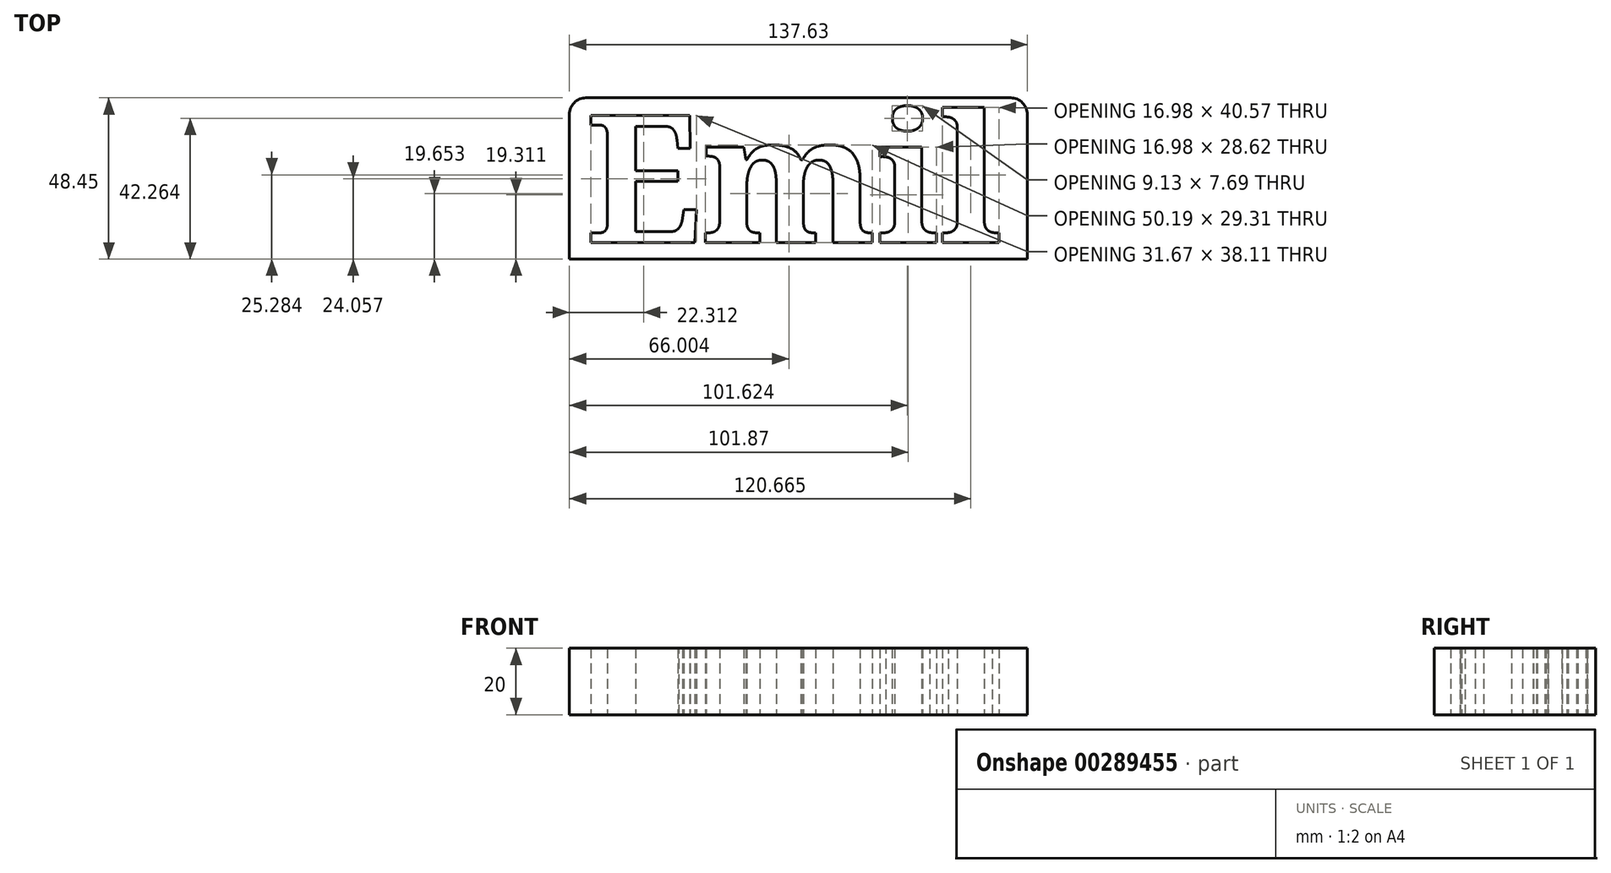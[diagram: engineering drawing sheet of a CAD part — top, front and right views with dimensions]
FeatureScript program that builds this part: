
annotation { "Feature Type Name" : "Feature", "Feature Type Description" : "" }
export const myFeature = defineFeature(function(context is Context, id is Id, definition is map)
    precondition{}
    {
        {
            var Q0;
            Q0=qCreatedBy(makeId("Top.planeOp"),FACE);
            var sketch = newSketch(context, id + "F0", { "sketchPlane" : qUnion([Q0])});
            skText(sketch, "E0", { "text": "Emil", "fontName": "NotoSerif-Bold.ttf"});
            skLineSegment(sketch, "E1.bottom", {"start": v(-68.2, 25) * mm, "end": v(69.44, 25) * mm});
            skLineSegment(sketch, "E1.top", {"start": v(-68.2, -23.44) * mm, "end": v(69.44, -23.44) * mm});
            skLineSegment(sketch, "E1.left", {"start": v(-68.2, 25) * mm, "end": v(-68.2, -23.44) * mm});
            skLineSegment(sketch, "E1.right", {"start": v(69.44, 25) * mm, "end": v(69.44, -23.44) * mm});
            const initialGuessF0  = {"E0": [-0.0632, -0.01844, 1, 0, 0.03844]};
            skSetInitialGuess(sketch, initialGuessF0);
            skSolve(sketch);
        }
        {
            var Q0;
            Q0 = qSketchRegion(id + "F0", true);
            extrude(context, id + "F1", {"entities" : qUnion([Q0]), "depth" : 20 * mm});
        }
        {
            var Q0;
            Q0=makeQuery(id+"F1.opExtrude","SWEPT_EDGE",EDGE,{"disambiguationData":[OSD([sQuery(id+"F0.wireOp",EDGE,"E1.bottom"),sQuery(id+"F0.wireOp",EDGE,"E1.left")])]});
            var Q1;
            Q1=makeQuery(id+"F1.opExtrude","SWEPT_EDGE",EDGE,{"disambiguationData":[OSD([sQuery(id+"F0.wireOp",EDGE,"E1.bottom"),sQuery(id+"F0.wireOp",EDGE,"E1.right")])]});
            fillet(context, id + "F2", {"entities" : qUnion([Q0, Q1]), "radius" : 5 * mm, "tangentPropagation" : true, "allowEdgeOverflow" : false});
        }
    });
